# Revit family: Sanitary_Toilets_Rak-Ceramics_RAK-MORNING-52-CM-WATER-CLOSET-RIMLESS-B
name_source: partatom
category: Plumbing Fixtures
revit_build: Autodesk Revit 2015 (Build: 20140606_1530(x64)
units: mm (PartAtom-declared; Revit-internal decimal feet)

## types (1)
- AK MORNING 52 CM WATER CLOSET RIMLESS BACK TO WALL
    BIMobject category = Toilets
    BIMobject category code = sanitary-toilets
    BIMobject main category = Sanitary
    BIMobject main category code = sanitary
    Brand url = https://www.rakceramics.com
    Date of publishing = 3/8/2019
    Default Elevation = 1219 mm
    Design country = United Arab Emirates
    Edition number = 1
    IFC Classification = Sanitary Terminal
    Installation instructions = https://www.rakceramics.com
    MEP Diameter = 100 mm
    Manufacturer = Rak Ceramics
    Manufacturer country = United Arab Emirates
    Manufacturer name = Rak Ceramics
    Material main = Ceramics
    Material secondary = Ceramics
    NBS Reference Code = 35-65-90-97
    NBS Reference Description = Wc Systems
    Nominal height = 420 mm  [stored 1.37795 ft]
    Nominal width = 365 mm  [stored 1.19751 ft]
    OmniClass Code = 23-31 19 19
    OmniClass Description = Water Closets
    Product Guid = 5fb19796-ae7b-4012-921e-b80b7f4dd218
    Product SKU = RAK-MORNING-WATER-CLOSET-RIMLESS-BACK-TO-WALL-P-S-TRAP-52CM-MORWC1346AWHA
    Product certification = https://www.rakceramics.com
    Product data url = https://bimobject.com
    Product family = MORNING
    Product group = Toilets
    Product url = https://www.rakceramics.com
    QR code = http://bimobject.com
    Technical description = https://www.rakceramics.com
    Uniclass 2.0 Code = SS-35-65-90-97
    Uniclass 2.0 Description = Wc Systems
    Weight Net (Kg) = 24
    Youtube clip = https://www.rakceramics.com

note: [stored X ft] marks values corroborated as IEEE doubles in the binary element streams (Revit-internal decimal feet)

## geometry (parser evidence)
native form markers: Sweep x3
no freeform markers — native parametric forms only
